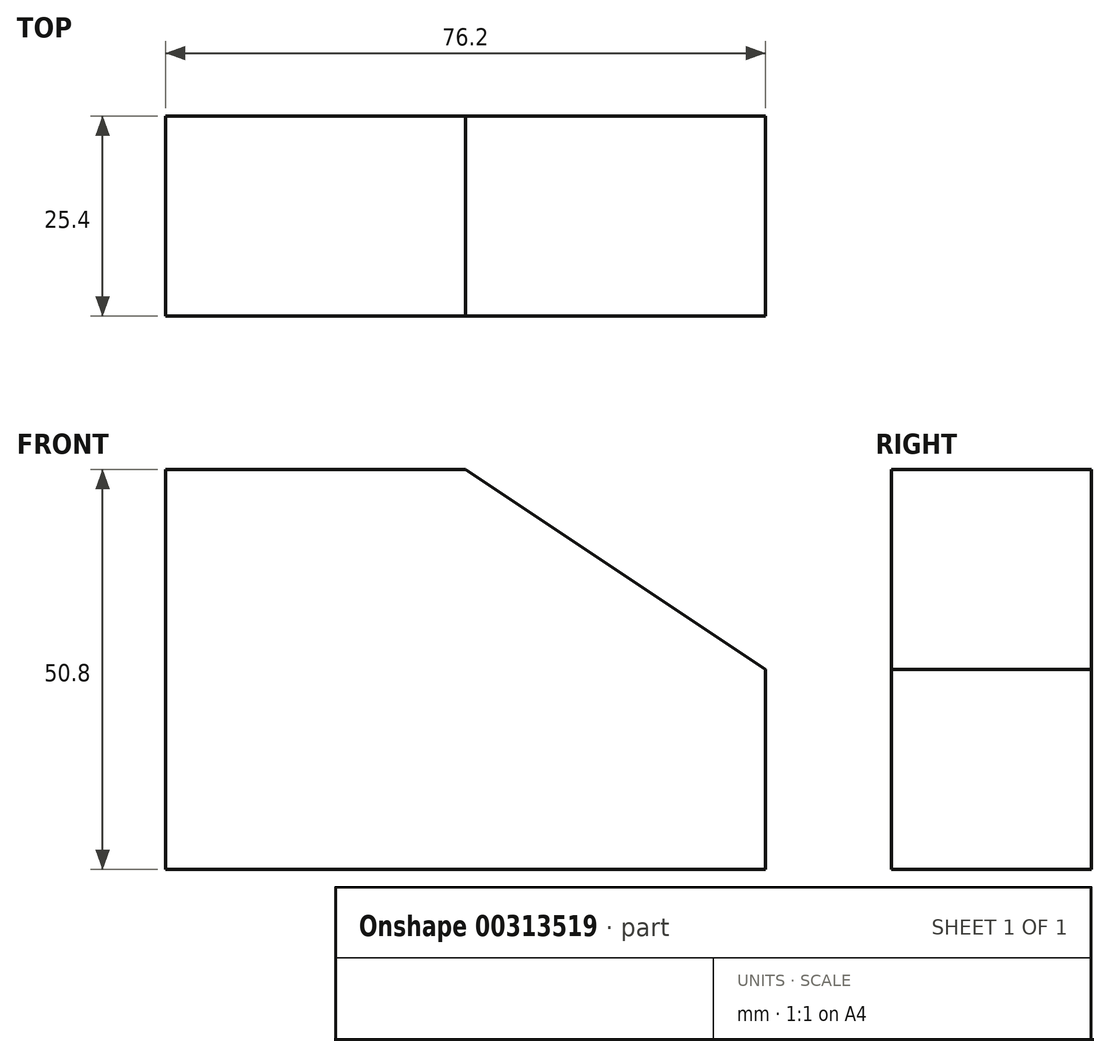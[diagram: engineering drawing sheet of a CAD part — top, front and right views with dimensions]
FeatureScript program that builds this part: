
annotation { "Feature Type Name" : "Feature", "Feature Type Description" : "" }
export const myFeature = defineFeature(function(context is Context, id is Id, definition is map)
    precondition{}
    {
        {
            var Q0;
            Q0=qCreatedBy(makeId("Front.planeOp"),FACE);
            var sketch = newSketch(context, id + "F0", { "sketchPlane" : qUnion([Q0])});
            skLineSegment(sketch, "E0", {"start": v(-50.16, 30.12) * mm, "end": v(-50.16, -20.68) * mm});
            skLineSegment(sketch, "E1", {"start": v(-50.16, -20.68) * mm, "end": v(26.04, -20.68) * mm});
            skLineSegment(sketch, "E2", {"start": v(26.04, -20.68) * mm, "end": v(26.04, 4.72) * mm});
            skLineSegment(sketch, "E3", {"start": v(26.04, 4.72) * mm, "end": v(-12.06, 30.12) * mm});
            skLineSegment(sketch, "E4", {"start": v(-12.06, 30.12) * mm, "end": v(-50.16, 30.12) * mm});
            skSolve(sketch);
        }
        {
            var Q0;
            Q0=makeQuery(id+"F0.imprint","IMPRINT",FACE,{"disambiguationData":[TD([[makeQuery(id+"F0.imprint","IMPRINT",EDGE,{"derivedFrom":sQuery(id+"F0.wireOp",EDGE,"E0")}),1.0]])]});
            extrude(context, id + "F1", {"entities" : qUnion([Q0]), "depth" : 25.4 * mm});
        }
    });
